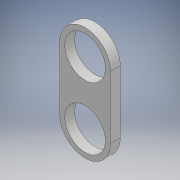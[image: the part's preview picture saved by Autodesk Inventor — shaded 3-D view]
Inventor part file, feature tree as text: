
AUTODESK INVENTOR PART (.ipt)
format: ipt  version: 2018 (Build 220112000, 112)  size: 113,664 bytes
history: native  units: mm
features: extrude x1, sketch x1
ambient origin geometry x8: Origin, YZ Plane, XZ Plane, XY Plane, X Axis, Y Axis, Z Axis, Center Point
bodies: Solide1 (feature_tree)
feature tree (2):
  extrude  "Extrusion1"  Depth=26.0mm
  sketch  "Esquisse1"
